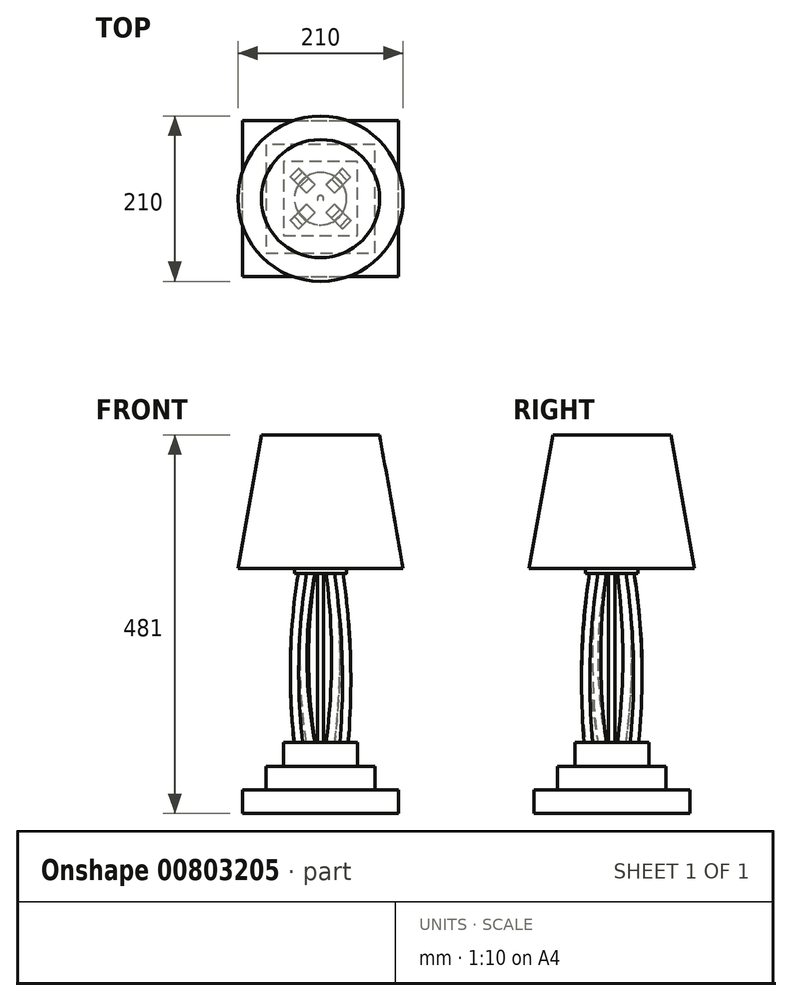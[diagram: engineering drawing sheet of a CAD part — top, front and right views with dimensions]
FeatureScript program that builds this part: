
annotation { "Feature Type Name" : "Feature", "Feature Type Description" : "" }
export const myFeature = defineFeature(function(context is Context, id is Id, definition is map)
    precondition{}
    {
        {
            var Q0;
            Q0=qCreatedBy(makeId("Top.planeOp"),FACE);
            var sketch = newSketch(context, id + "F0", { "sketchPlane" : qUnion([Q0])});
            skLineSegment(sketch, "E0.bottom", {"start": v(0, 0) * mm, "end": v(198, 0) * mm});
            skLineSegment(sketch, "E0.top", {"start": v(0, 198) * mm, "end": v(198, 198) * mm});
            skLineSegment(sketch, "E0.left", {"start": v(0, 0) * mm, "end": v(0, 198) * mm});
            skLineSegment(sketch, "E0.right", {"start": v(198, 0) * mm, "end": v(198, 198) * mm});
            skSolve(sketch);
        }
        {
            var Q0;
            Q0 = qSketchRegion(id + "F0", true);
            extrude(context, id + "F1", {"entities" : qUnion([Q0]), "depth" : 30 * mm, "offsetDistance" : 25 * mm});
        }
        {
            var Q0;
            Q0=makeQuery(id+"F1.opExtrude","CAP_FACE",FACE,{"disambiguationData":[OSD([sQuery(id+"F0.wireOp",EDGE,"E0.bottom"),sQuery(id+"F0.wireOp",EDGE,"E0.top"),sQuery(id+"F0.wireOp",EDGE,"E0.left"),sQuery(id+"F0.wireOp",EDGE,"E0.right")])],"isStart":false});
            var sketch = newSketch(context, id + "F2", { "sketchPlane" : qUnion([Q0])});
            skLineSegment(sketch, "E1.0", {"start": v(168, 168) * mm, "end": v(30, 168) * mm});
            skLineSegment(sketch, "E1.1", {"start": v(168, 30) * mm, "end": v(168, 168) * mm});
            skLineSegment(sketch, "E1.2", {"start": v(30, 30) * mm, "end": v(168, 30) * mm});
            skLineSegment(sketch, "E1.3", {"start": v(30, 168) * mm, "end": v(30, 30) * mm});
            skSolve(sketch);
        }
        {
            var Q0;
            Q0=makeQuery(id+"F2.imprint","IMPRINT",FACE,{"disambiguationData":[TD([[makeQuery(id+"F2.imprint","IMPRINT",EDGE,{"derivedFrom":sQuery(id+"F2.wireOp",EDGE,"E1.0")}),1.0]])]});
            extrude(context, id + "F3", {"entities" : qUnion([Q0]), "operationType" : NewBodyOperationType.ADD, "depth" : 30 * mm, "offsetDistance" : 25 * mm});
        }
        {
            var Q0;
            Q0=makeQuery(id+"F3.opExtrude","CAP_FACE",FACE,{"disambiguationData":[OSD([sQuery(id+"F2.wireOp",EDGE,"E1.0"),sQuery(id+"F2.wireOp",EDGE,"E1.1"),sQuery(id+"F2.wireOp",EDGE,"E1.2"),sQuery(id+"F2.wireOp",EDGE,"E1.3")])],"isStart":false});
            var sketch = newSketch(context, id + "F4", { "sketchPlane" : qUnion([Q0])});
            skLineSegment(sketch, "E2.0", {"start": v(146, 146) * mm, "end": v(52, 146) * mm});
            skLineSegment(sketch, "E2.1", {"start": v(146, 52) * mm, "end": v(146, 146) * mm});
            skLineSegment(sketch, "E2.2", {"start": v(52, 52) * mm, "end": v(146, 52) * mm});
            skLineSegment(sketch, "E2.3", {"start": v(52, 146) * mm, "end": v(52, 52) * mm});
            skSolve(sketch);
        }
        {
            var Q0;
            Q0=makeQuery(id+"F4.imprint","IMPRINT",FACE,{"disambiguationData":[TD([[makeQuery(id+"F4.imprint","IMPRINT",EDGE,{"derivedFrom":sQuery(id+"F4.wireOp",EDGE,"E2.0")}),1.0]])]});
            extrude(context, id + "F5", {"entities" : qUnion([Q0]), "operationType" : NewBodyOperationType.ADD, "depth" : 30 * mm, "offsetDistance" : 25 * mm});
        }
        {
            var Q0;
            Q0=makeQuery(id+"F5.opExtrude","CAP_FACE",FACE,{"disambiguationData":[OSD([sQuery(id+"F4.wireOp",EDGE,"E2.0"),sQuery(id+"F4.wireOp",EDGE,"E2.1"),sQuery(id+"F4.wireOp",EDGE,"E2.2"),sQuery(id+"F4.wireOp",EDGE,"E2.3")])],"isStart":false});
            var sketch = newSketch(context, id + "F6", { "sketchPlane" : qUnion([Q0])});
            skCircle(sketch, "E3", {"center": v(99, 99) * mm, "radius": 4 * mm});
            skPoint(sketch, "E3.centerSnap0", {"position": v(52, 99) * mm});
            skPoint(sketch, "E3.centerSnap1", {"position": v(99, 52) * mm});
            skSolve(sketch);
        }
        {
            var Q0;
            Q0 = qSketchRegion(id + "F6", true);
            extrude(context, id + "F7", {"entities" : qUnion([Q0]), "operationType" : NewBodyOperationType.ADD, "depth" : 215 * mm, "offsetDistance" : 25 * mm});
        }
        {
            var Q0;
            Q0=makeQuery(id+"F5.opExtrude","CAP_FACE",FACE,{"disambiguationData":[OSD([sQuery(id+"F4.wireOp",EDGE,"E2.0"),sQuery(id+"F4.wireOp",EDGE,"E2.1"),sQuery(id+"F4.wireOp",EDGE,"E2.2"),sQuery(id+"F4.wireOp",EDGE,"E2.3")])],"isStart":false});
            var sketch = newSketch(context, id + "F8", { "sketchPlane" : qUnion([Q0])});
            skLineSegment(sketch, "E4", {"start": v(65.41, 132.59) * mm, "end": v(146, 52) * mm});
            skLineSegment(sketch, "E5", {"start": v(146, 52) * mm, "end": v(52, 52) * mm});
            skLineSegment(sketch, "E6", {"start": v(52, 52) * mm, "end": v(146, 146) * mm});
            skLineSegment(sketch, "E7.0", {"start": v(46.7, 140.7) * mm, "end": v(47, 140.4) * mm});
            skLineSegment(sketch, "E8.0", {"start": v(57.3, 151.3) * mm, "end": v(57.6, 151) * mm});
            skLineSegment(sketch, "E9.0", {"start": v(57.3, 46.7) * mm, "end": v(151.3, 140.7) * mm});
            skLineSegment(sketch, "E10.0", {"start": v(46.7, 57.3) * mm, "end": v(140.7, 151.3) * mm});
            skLineSegment(sketch, "E11.0", {"start": v(39.63, 64.37) * mm, "end": v(74.25, 99) * mm});
            skLineSegment(sketch, "E12.0", {"start": v(64.37, 39.63) * mm, "end": v(158.37, 133.63) * mm});
            skLineSegment(sketch, "E13.0", {"start": v(151, 151) * mm, "end": v(47, 151) * mm});
            skLineSegment(sketch, "E13.1", {"start": v(151, 47) * mm, "end": v(151, 151) * mm});
            skLineSegment(sketch, "E13.2", {"start": v(47, 47) * mm, "end": v(151, 47) * mm});
            skLineSegment(sketch, "E13.3", {"start": v(47, 151) * mm, "end": v(47, 47) * mm});
            skLineSegment(sketch, "E14.0", {"start": v(18.41, 85.59) * mm, "end": v(47, 114.18) * mm});
            skLineSegment(sketch, "E15.0", {"start": v(85.59, 18.41) * mm, "end": v(179.59, 112.41) * mm});
            skLineSegment(sketch, "E16.0", {"start": v(39.63, 133.63) * mm, "end": v(47, 126.25) * mm});
            skLineSegment(sketch, "E17.0", {"start": v(64.37, 158.37) * mm, "end": v(158.37, 64.37) * mm});
            skLineSegment(sketch, "E18.0", {"start": v(85.59, 179.59) * mm, "end": v(179.59, 85.59) * mm});
            skLineSegment(sketch, "E19.0", {"start": v(18.41, 112.41) * mm, "end": v(112.41, 18.41) * mm});
            skLineSegment(sketch, "E20.trimOffspring", {"start": v(77.79, 144.96) * mm, "end": v(112.41, 179.59) * mm});
            skLineSegment(sketch, "E21.trimOffspring", {"start": v(70.72, 137.9) * mm, "end": v(91.93, 116.68) * mm});
            skLineSegment(sketch, "E22.trimOffspring", {"start": v(60.1, 127.28) * mm, "end": v(81.32, 106.07) * mm});
            skLineSegment(sketch, "E23.trimOffspring", {"start": v(74.25, 99) * mm, "end": v(133.63, 39.63) * mm});
            skLineSegment(sketch, "E24.trimOffspring", {"start": v(60.1, 127.28) * mm, "end": v(70.72, 137.9) * mm});
            skLineSegment(sketch, "E25.trimOffspring", {"start": v(81.32, 106.07) * mm, "end": v(91.93, 116.68) * mm});
            skLineSegment(sketch, "E26.trimOffspring", {"start": v(88.4, 99) * mm, "end": v(140.7, 46.7) * mm});
            skLineSegment(sketch, "E27.trimOffspring", {"start": v(99, 109.6) * mm, "end": v(151.3, 57.3) * mm});
            skLineSegment(sketch, "E28.trimOffspring", {"start": v(99, 123.75) * mm, "end": v(133.63, 158.37) * mm});
            skSolve(sketch);
        }
        {
            var Q0;
            {var subQ5=sQuery(id+"F8.wireOp",EDGE,"E22.trimOffspring");Q0=makeQuery(id+"F8.imprint","IMPRINT",FACE,{"disambiguationData":[TD([[makeQuery(id+"F8.imprint","IMPRINT",EDGE,{"derivedFrom":subQ5}),1.0]])]});}
            var Q1;
            {var subQ5=sQuery(id+"F8.wireOp",EDGE,"E21.trimOffspring");Q1=makeQuery(id+"F8.imprint","IMPRINT",FACE,{"disambiguationData":[TD([[makeQuery(id+"F8.imprint","IMPRINT",EDGE,{"derivedFrom":subQ5}),-1.0]])]});}
            var Q2;
            {var subQ0=sQuery(id+"F8.wireOp",EDGE,"E17.0");var subQ1=sQuery(id+"F8.wireOp",EDGE,"E6");var subQ2=makeQuery(id+"F8.imprint","INTERSECT",VERTEX,{"derivedFrom":[subQ1,subQ0]});Q2=makeQuery(id+"F8.imprint","IMPRINT",FACE,{"disambiguationData":[TD([[makeQuery(id+"F8.imprint","IMPRINT",EDGE,{"disambiguationData":[TD([[subQ2,-1.0]])],"derivedFrom":subQ1}),1.0]])]});}
            var Q3;
            {var subQ0=sQuery(id+"F8.wireOp",EDGE,"E17.0");var subQ1=sQuery(id+"F8.wireOp",EDGE,"E6");var subQ2=makeQuery(id+"F8.imprint","INTERSECT",VERTEX,{"derivedFrom":[subQ1,subQ0]});Q3=makeQuery(id+"F8.imprint","IMPRINT",FACE,{"disambiguationData":[TD([[makeQuery(id+"F8.imprint","IMPRINT",EDGE,{"disambiguationData":[TD([[subQ2,-1.0]])],"derivedFrom":subQ1}),-1.0]])]});}
            var Q4;
            {var subQ0=sQuery(id+"F8.wireOp",EDGE,"E12.0");var subQ1=sQuery(id+"F8.wireOp",EDGE,"E4");var subQ2=makeQuery(id+"F8.imprint","INTERSECT",VERTEX,{"derivedFrom":[subQ1,subQ0]});Q4=makeQuery(id+"F8.imprint","IMPRINT",FACE,{"disambiguationData":[TD([[makeQuery(id+"F8.imprint","IMPRINT",EDGE,{"disambiguationData":[TD([[subQ2,-1.0]])],"derivedFrom":subQ1}),1.0]])]});}
            var Q5;
            {var subQ0=sQuery(id+"F8.wireOp",EDGE,"E12.0");var subQ1=sQuery(id+"F8.wireOp",EDGE,"E4");var subQ2=makeQuery(id+"F8.imprint","INTERSECT",VERTEX,{"derivedFrom":[subQ1,subQ0]});Q5=makeQuery(id+"F8.imprint","IMPRINT",FACE,{"disambiguationData":[TD([[makeQuery(id+"F8.imprint","IMPRINT",EDGE,{"disambiguationData":[TD([[subQ2,-1.0]])],"derivedFrom":subQ1}),-1.0]])]});}
            var Q6;
            {var subQ0=sQuery(id+"F8.wireOp",EDGE,"E19.0");var subQ1=sQuery(id+"F8.wireOp",EDGE,"E6");var subQ2=makeQuery(id+"F8.imprint","INTERSECT",VERTEX,{"derivedFrom":[subQ1,subQ0]});Q6=makeQuery(id+"F8.imprint","IMPRINT",FACE,{"disambiguationData":[TD([[makeQuery(id+"F8.imprint","IMPRINT",EDGE,{"disambiguationData":[TD([[subQ2,-1.0]])],"derivedFrom":subQ1}),-1.0]])]});}
            var Q7;
            {var subQ0=sQuery(id+"F8.wireOp",EDGE,"E19.0");var subQ1=sQuery(id+"F8.wireOp",EDGE,"E6");var subQ2=makeQuery(id+"F8.imprint","INTERSECT",VERTEX,{"derivedFrom":[subQ1,subQ0]});Q7=makeQuery(id+"F8.imprint","IMPRINT",FACE,{"disambiguationData":[TD([[makeQuery(id+"F8.imprint","IMPRINT",EDGE,{"disambiguationData":[TD([[subQ2,-1.0]])],"derivedFrom":subQ1}),1.0]])]});}
            extrude(context, id + "F9", {"entities" : qUnion([Q0, Q1, Q2, Q3, Q4, Q5, Q6, Q7]), "operationType" : NewBodyOperationType.ADD, "depth" : 215 * mm, "offsetDistance" : 25 * mm});
        }
        {
            var Q0;
            {var subQ0=sQuery(id+"F8.wireOp",EDGE,"E9.0");Q0=makeQuery(id+"F9.opExtrude","SWEPT_FACE",FACE,{"disambiguationData":[OSD([subQ0]),TDD([makeQuery(id+"F8.imprint","IMPRINT",EDGE,{"disambiguationData":[TD([[makeQuery(id+"F8.imprint","INTERSECT",VERTEX,{"derivedFrom":[subQ0,sQuery(id+"F8.wireOp",EDGE,"E19.0")]}),-1.0]])],"derivedFrom":subQ0})])]});}
            var sketch = newSketch(context, id + "F10", { "sketchPlane" : qUnion([Q0])});
            skArc(sketch, "E29", {"start": v(122.5, 305) * mm, "mid": v(108.14, 197.5) * mm, "end": v(122.5, 90) * mm});
            skLineSegment(sketch, "E30", {"start": v(107.5, 305) * mm, "end": v(122.5, 305) * mm});
            skLineSegment(sketch, "E31", {"start": v(122.5, 90) * mm, "end": v(107.5, 90) * mm});
            skArc(sketch, "E32", {"start": v(107.5, 305) * mm, "mid": v(93.53, 197.84) * mm, "end": v(100.53, 90) * mm});
            skSolve(sketch);
        }
        {
            var Q0;
            Q0 = qSketchRegion(id + "F10", true);
            var Q1;
            Q1=makeQuery(id+"F10.imprint","IMPRINT",FACE,{"disambiguationData":[TD([[makeQuery(id+"F10.imprint","IMPRINT",EDGE,{"derivedFrom":sQuery(id+"F10.wireOp",EDGE,"E29")}),1.0]])]});
            var Q2;
            {var subQ0=sQuery(id+"F10.wireOp",EDGE,"E32");Q2=makeQuery(id+"F10.imprint","IMPRINT",FACE,{"disambiguationData":[TD([[makeQuery(id+"F10.imprint","IMPRINT",EDGE,{"derivedFrom":subQ0}),-1.0]])]});}
            extrude(context, id + "F11", {"entities" : qUnion([Q0, Q1, Q2]), "operationType" : NewBodyOperationType.REMOVE, "oppositeDirection" : true, "depth" : 25 * mm, "offsetDistance" : 25 * mm});
        }
        {
            var Q0;
            Q0=makeQuery(id+"F9.opExtrude","SWEPT_FACE",FACE,{"disambiguationData":[OSD([sQuery(id+"F8.wireOp",EDGE,"E21.trimOffspring")])]});
            var sketch = newSketch(context, id + "F12", { "sketchPlane" : qUnion([Q0])});
            skArc(sketch, "E33", {"start": v(17.5, 90) * mm, "mid": v(28.99, 197.5) * mm, "end": v(17.5, 305) * mm});
            skArc(sketch, "E34", {"start": v(39.96, 90) * mm, "mid": v(46.51, 197.86) * mm, "end": v(32.5, 305) * mm});
            skLineSegment(sketch, "E35", {"start": v(17.5, 305) * mm, "end": v(32.5, 305) * mm});
            skLineSegment(sketch, "E36", {"start": v(39.96, 90) * mm, "end": v(17.5, 90) * mm});
            skSolve(sketch);
        }
        {
            var Q0;
            Q0=makeQuery(id+"F12.imprint","IMPRINT",FACE,{"disambiguationData":[TD([[makeQuery(id+"F12.imprint","IMPRINT",EDGE,{"derivedFrom":sQuery(id+"F12.wireOp",EDGE,"E33")}),1.0]])]});
            var Q1;
            {var subQ0=sQuery(id+"F12.wireOp",EDGE,"E34");Q1=makeQuery(id+"F12.imprint","IMPRINT",FACE,{"disambiguationData":[TD([[makeQuery(id+"F12.imprint","IMPRINT",EDGE,{"derivedFrom":subQ0}),-1.0]])]});}
            extrude(context, id + "F13", {"entities" : qUnion([Q0, Q1]), "operationType" : NewBodyOperationType.REMOVE, "oppositeDirection" : true, "depth" : 25 * mm, "offsetDistance" : 25 * mm});
        }
        {
            var Q0;
            {var subQ0=sQuery(id+"F8.wireOp",EDGE,"E9.0");Q0=makeQuery(id+"F9.opExtrude","SWEPT_FACE",FACE,{"disambiguationData":[OSD([subQ0]),TDD([makeQuery(id+"F8.imprint","IMPRINT",EDGE,{"disambiguationData":[TD([[makeQuery(id+"F8.imprint","INTERSECT",VERTEX,{"derivedFrom":[subQ0,sQuery(id+"F8.wireOp",EDGE,"E17.0")]}),-1.0]])],"derivedFrom":subQ0})])]});}
            var sketch = newSketch(context, id + "F14", { "sketchPlane" : qUnion([Q0])});
            skArc(sketch, "E37", {"start": v(157.5, 90) * mm, "mid": v(167.32, 197.5) * mm, "end": v(157.5, 305) * mm});
            skArc(sketch, "E38", {"start": v(180.44, 90) * mm, "mid": v(186.26, 197.86) * mm, "end": v(172.5, 305) * mm});
            skLineSegment(sketch, "E39", {"start": v(157.5, 305) * mm, "end": v(172.5, 305) * mm});
            skLineSegment(sketch, "E40", {"start": v(157.5, 90) * mm, "end": v(180.44, 90) * mm});
            skSolve(sketch);
        }
        {
            var Q0;
            {var subQ0=sQuery(id+"F14.wireOp",EDGE,"E38");Q0=makeQuery(id+"F14.imprint","IMPRINT",FACE,{"disambiguationData":[TD([[makeQuery(id+"F14.imprint","IMPRINT",EDGE,{"derivedFrom":subQ0}),-1.0]])]});}
            var Q1;
            Q1=makeQuery(id+"F14.imprint","IMPRINT",FACE,{"disambiguationData":[TD([[makeQuery(id+"F14.imprint","IMPRINT",EDGE,{"derivedFrom":sQuery(id+"F14.wireOp",EDGE,"E37")}),1.0]])]});
            extrude(context, id + "F15", {"entities" : qUnion([Q0, Q1]), "operationType" : NewBodyOperationType.REMOVE, "oppositeDirection" : true, "depth" : 25 * mm, "offsetDistance" : 25 * mm});
        }
        {
            var Q0;
            Q0=makeQuery(id+"F9.opExtrude","SWEPT_FACE",FACE,{"disambiguationData":[OSD([sQuery(id+"F8.wireOp",EDGE,"E27.trimOffspring")])]});
            var sketch = newSketch(context, id + "F16", { "sketchPlane" : qUnion([Q0])});
            skArc(sketch, "E41", {"start": v(-17.5, 305) * mm, "mid": v(-27.24, 197.5) * mm, "end": v(-17.5, 90) * mm});
            skArc(sketch, "E42", {"start": v(-32.5, 305) * mm, "mid": v(-46.24, 197.9) * mm, "end": v(-42.13, 90) * mm});
            skLineSegment(sketch, "E43", {"start": v(-32.5, 305) * mm, "end": v(-17.5, 305) * mm});
            skLineSegment(sketch, "E44", {"start": v(-42.13, 90) * mm, "end": v(-17.5, 90) * mm});
            skSolve(sketch);
        }
        {
            var Q0;
            {var subQ0=sQuery(id+"F16.wireOp",EDGE,"E42");Q0=makeQuery(id+"F16.imprint","IMPRINT",FACE,{"disambiguationData":[TD([[makeQuery(id+"F16.imprint","IMPRINT",EDGE,{"derivedFrom":subQ0}),-1.0]])]});}
            var Q1;
            Q1=makeQuery(id+"F16.imprint","IMPRINT",FACE,{"disambiguationData":[TD([[makeQuery(id+"F16.imprint","IMPRINT",EDGE,{"derivedFrom":sQuery(id+"F16.wireOp",EDGE,"E41")}),1.0]])]});
            extrude(context, id + "F17", {"entities" : qUnion([Q0, Q1]), "operationType" : NewBodyOperationType.REMOVE, "oppositeDirection" : true, "depth" : 25 * mm, "offsetDistance" : 25 * mm});
        }
        {
            var Q0;
            Q0=makeQuery(id+"F7.opExtrude","CAP_FACE",FACE,{"disambiguationData":[OSD([sQuery(id+"F6.wireOp",EDGE,"E3")])],"isStart":false});
            var sketch = newSketch(context, id + "F18", { "sketchPlane" : qUnion([Q0])});
            skCircle(sketch, "E45", {"center": v(99, 99) * mm, "radius": 33.26 * mm});
            skSolve(sketch);
        }
        {
            var Q0;
            Q0 = qSketchRegion(id + "F18", true);
            extrude(context, id + "F19", {"entities" : qUnion([Q0]), "operationType" : NewBodyOperationType.ADD, "depth" : 6 * mm, "offsetDistance" : 25 * mm});
        }
        {
            var Q0;
            Q0=makeQuery(id+"F19.opExtrude","CAP_FACE",FACE,{"disambiguationData":[OSD([sQuery(id+"F18.wireOp",EDGE,"E45")])],"isStart":false});
            var sketch = newSketch(context, id + "F20", { "sketchPlane" : qUnion([Q0])});
            skCircle(sketch, "E46", {"center": v(99, 99) * mm, "radius": 105 * mm});
            skSolve(sketch);
        }
        {
            var Q0;
            Q0=makeQuery(id+"F20.imprint","IMPRINT",FACE,{"disambiguationData":[TD([[makeQuery(id+"F20.imprint","IMPRINT",EDGE,{"derivedFrom":makeQuery(id+"F19.opExtrude","CAP_EDGE",EDGE,{"disambiguationData":[OSD([sQuery(id+"F18.wireOp",EDGE,"E45")])],"isStart":false})}),1.0]])]});
            var Q1;
            Q1=makeQuery(id+"F20.imprint","IMPRINT",FACE,{"disambiguationData":[TD([[makeQuery(id+"F20.imprint","IMPRINT",EDGE,{"derivedFrom":sQuery(id+"F20.wireOp",EDGE,"E46")}),1.0]])]});
            extrude(context, id + "F21", {"entities" : qUnion([Q0, Q1]), "operationType" : NewBodyOperationType.ADD, "depth" : 170 * mm, "offsetDistance" : 25 * mm, "hasDraft" : true, "draftAngle" : 10 * degree, "draftPullDirection" : true});
        }
    });
